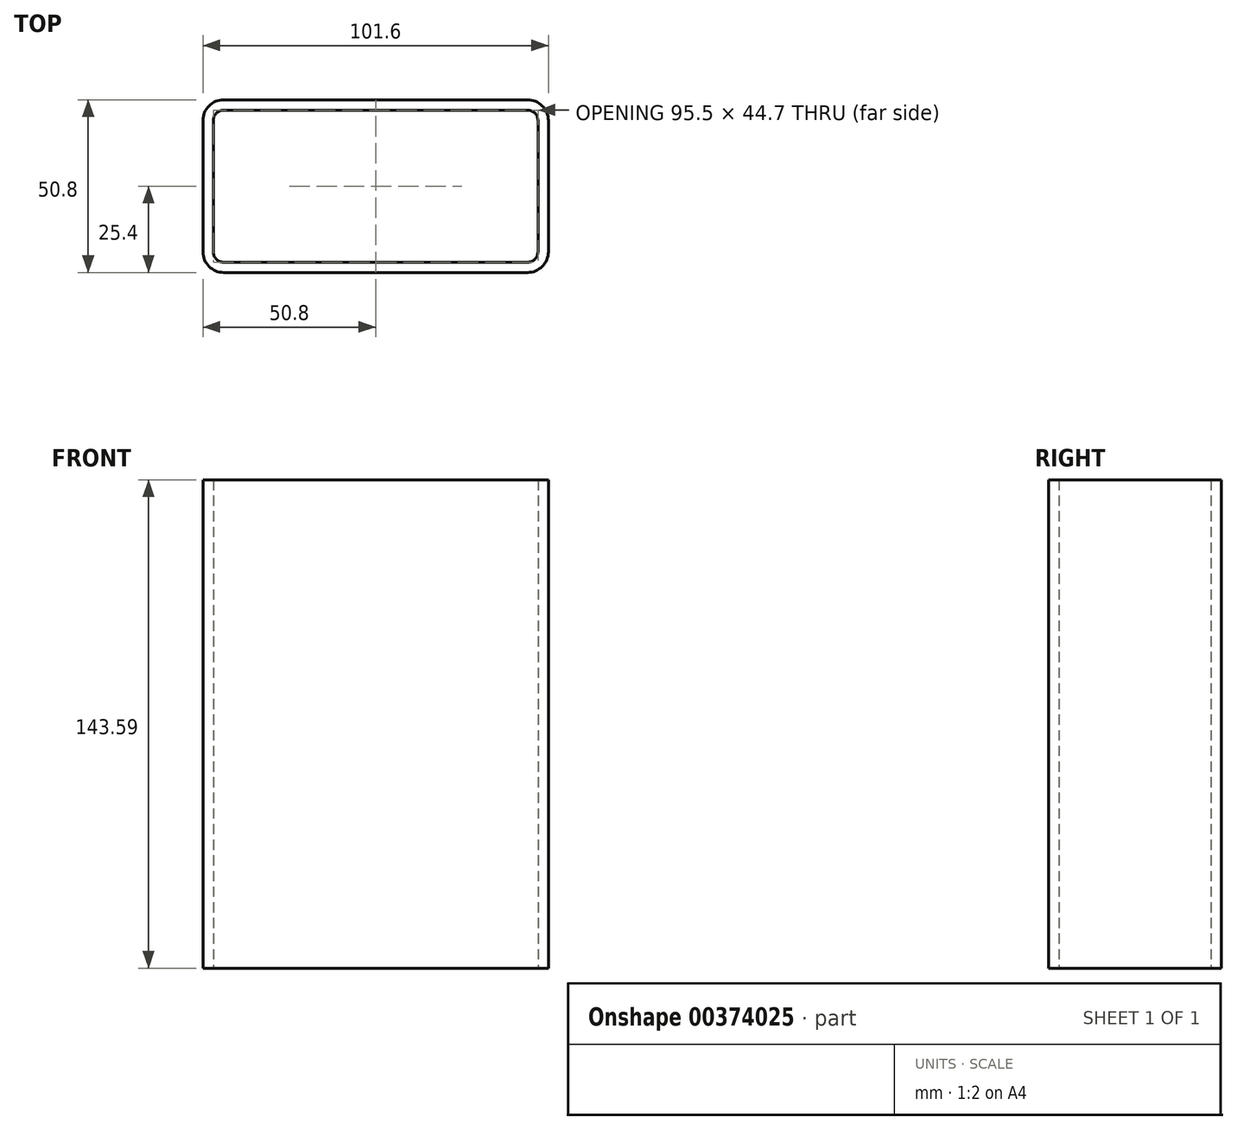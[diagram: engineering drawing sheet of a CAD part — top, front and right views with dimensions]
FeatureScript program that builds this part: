
annotation { "Feature Type Name" : "Feature", "Feature Type Description" : "" }
export const myFeature = defineFeature(function(context is Context, id is Id, definition is map)
    precondition{}
    {
        {
            var Q0;
            Q0=qCreatedBy(makeId("Top.planeOp"),FACE);
            var sketch = newSketch(context, id + "F0", { "sketchPlane" : qUnion([Q0])});
            skLineSegment(sketch, "E0.bottom", {"start": v(6.1, 0) * mm, "end": v(95.5, 0) * mm});
            skLineSegment(sketch, "E0.top", {"start": v(6.1, 50.8) * mm, "end": v(95.5, 50.8) * mm});
            skLineSegment(sketch, "E0.left", {"start": v(0, 6.1) * mm, "end": v(0, 44.7) * mm});
            skLineSegment(sketch, "E0.right", {"start": v(101.6, 6.1) * mm, "end": v(101.6, 44.7) * mm});
            skLineSegment(sketch, "E1.bottom", {"start": v(6.1, 47.75) * mm, "end": v(95.5, 47.75) * mm});
            skLineSegment(sketch, "E1.top", {"start": v(6.1, 3.05) * mm, "end": v(95.5, 3.05) * mm});
            skLineSegment(sketch, "E1.left", {"start": v(3.05, 44.7) * mm, "end": v(3.05, 6.1) * mm});
            skLineSegment(sketch, "E1.right", {"start": v(98.55, 44.7) * mm, "end": v(98.55, 6.1) * mm});
            skPoint(sketch, "E2.visualSharp", {"position": v(3.05, 47.75) * mm});
            skArc(sketch, "E2.filletArc", {"start": v(6.1, 47.75) * mm, "mid": v(3.94, 46.86) * mm, "end": v(3.05, 44.7) * mm});
            skPoint(sketch, "E3.visualSharp", {"position": v(98.55, 47.75) * mm});
            skArc(sketch, "E3.filletArc", {"start": v(98.55, 44.7) * mm, "mid": v(97.66, 46.86) * mm, "end": v(95.5, 47.75) * mm});
            skPoint(sketch, "E4.visualSharp", {"position": v(98.55, 3.05) * mm});
            skArc(sketch, "E4.filletArc", {"start": v(95.5, 3.05) * mm, "mid": v(97.66, 3.94) * mm, "end": v(98.55, 6.1) * mm});
            skPoint(sketch, "E5.visualSharp", {"position": v(3.05, 3.05) * mm});
            skArc(sketch, "E5.filletArc", {"start": v(3.05, 6.1) * mm, "mid": v(3.94, 3.94) * mm, "end": v(6.1, 3.05) * mm});
            skPoint(sketch, "E6.visualSharp", {"position": v(0, 50.8) * mm});
            skArc(sketch, "E6.filletArc", {"start": v(6.1, 50.8) * mm, "mid": v(1.79, 49.01) * mm, "end": v(0, 44.7) * mm});
            skPoint(sketch, "E7.visualSharp", {"position": v(101.6, 50.8) * mm});
            skArc(sketch, "E7.filletArc", {"start": v(101.6, 44.7) * mm, "mid": v(99.81, 49.01) * mm, "end": v(95.5, 50.8) * mm});
            skPoint(sketch, "E8.visualSharp", {"position": v(101.6, 0) * mm});
            skArc(sketch, "E8.filletArc", {"start": v(95.5, 0) * mm, "mid": v(99.81, 1.79) * mm, "end": v(101.6, 6.1) * mm});
            skPoint(sketch, "E9.visualSharp", {"position": v(0, 0) * mm});
            skArc(sketch, "E9.filletArc", {"start": v(0, 6.1) * mm, "mid": v(1.79, 1.79) * mm, "end": v(6.1, 0) * mm});
            skSolve(sketch);
        }
        {
            var Q0;
            Q0 = qSketchRegion(id + "F0", true);
            extrude(context, id + "F1", {"entities" : qUnion([Q0]), "depth" : 143.6 * mm, "offsetDistance" : 25 * mm});
        }
    });
